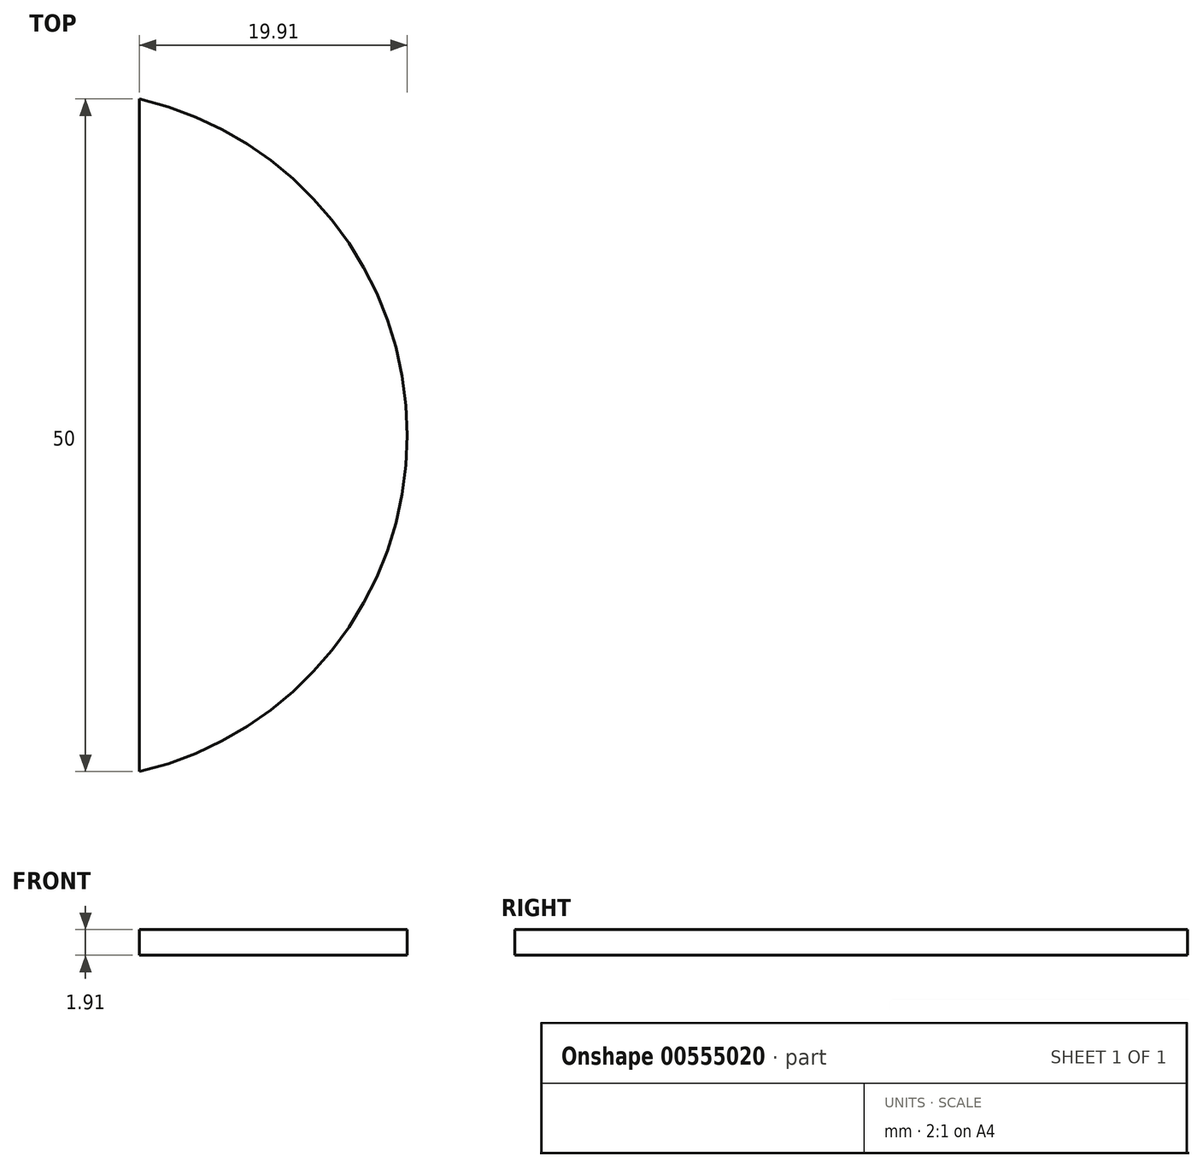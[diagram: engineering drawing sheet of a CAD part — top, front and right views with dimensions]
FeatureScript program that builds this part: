
annotation { "Feature Type Name" : "Feature", "Feature Type Description" : "" }
export const myFeature = defineFeature(function(context is Context, id is Id, definition is map)
    precondition{}
    {
        {
            var Q0;
            Q0=qCreatedBy(makeId("Top.planeOp"),FACE);
            var sketch = newSketch(context, id + "F0", { "sketchPlane" : qUnion([Q0])});
            skLineSegment(sketch, "E0", {"start": v(0, 0) * mm, "end": v(0, 50) * mm});
            skArc(sketch, "E1", {"start": v(0, 0) * mm, "mid": v(19.9, 25) * mm, "end": v(0, 50) * mm});
            skSolve(sketch);
        }
        {
            var Q0;
            Q0=makeQuery(id+"F0.imprint","IMPRINT",FACE,{"disambiguationData":[TD([[makeQuery(id+"F0.imprint","IMPRINT",EDGE,{"derivedFrom":sQuery(id+"F0.wireOp",EDGE,"E0")}),-1.0]])]});
            extrude(context, id + "F1", {"entities" : qUnion([Q0]), "depth" : 1.9 * mm, "offsetDistance" : 25.4 * mm});
        }
    });
